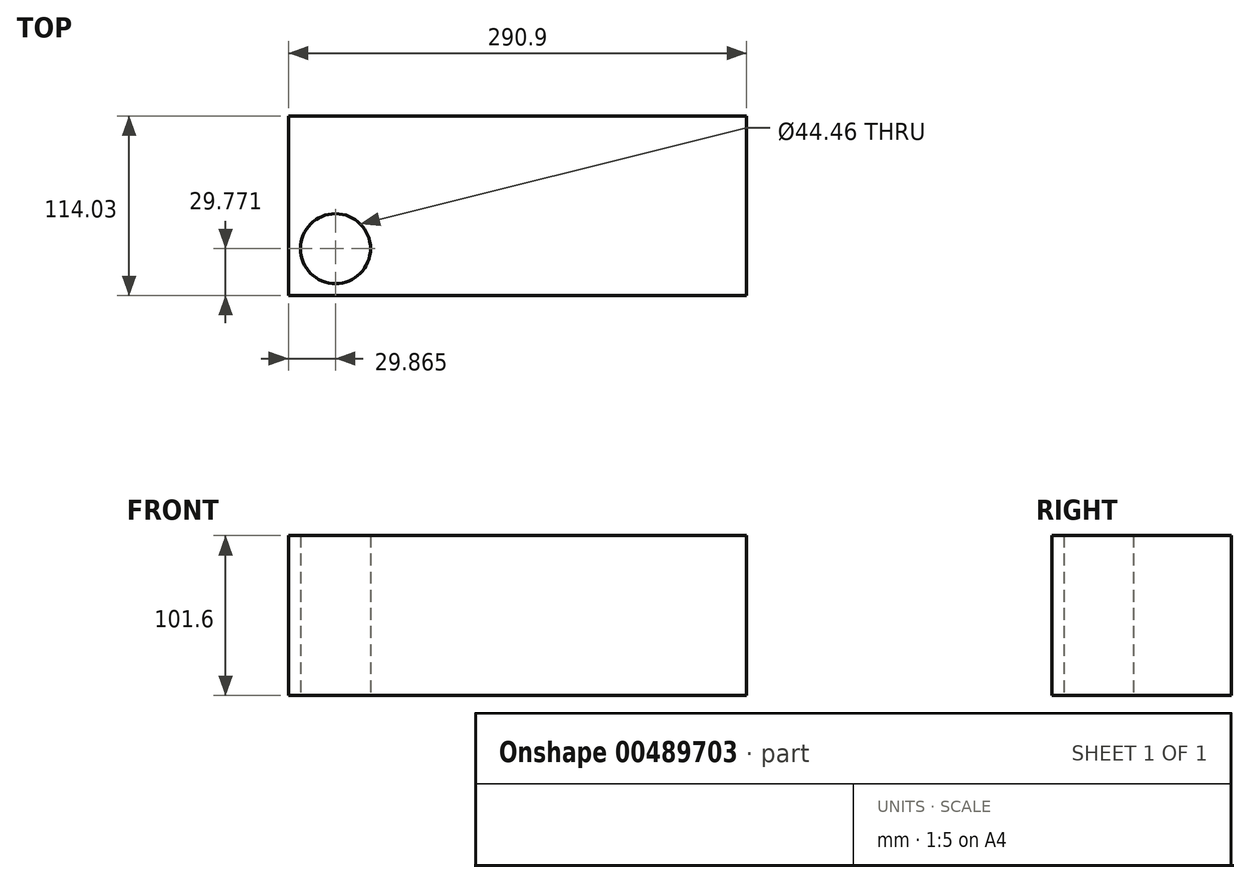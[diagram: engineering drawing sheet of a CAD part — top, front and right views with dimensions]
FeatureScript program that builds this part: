
annotation { "Feature Type Name" : "Feature", "Feature Type Description" : "" }
export const myFeature = defineFeature(function(context is Context, id is Id, definition is map)
    precondition{}
    {
        {
            var Q0;
            Q0=qCreatedBy(makeId("Top.planeOp"),FACE);
            var sketch = newSketch(context, id + "F0", { "sketchPlane" : qUnion([Q0])});
            skLineSegment(sketch, "E0.bottom", {"start": v(-66.27, 50.65) * mm, "end": v(224.63, 50.65) * mm});
            skLineSegment(sketch, "E0.top", {"start": v(-66.27, -63.38) * mm, "end": v(224.63, -63.38) * mm});
            skLineSegment(sketch, "E0.left", {"start": v(-66.27, 50.65) * mm, "end": v(-66.27, -63.38) * mm});
            skLineSegment(sketch, "E0.right", {"start": v(224.63, 50.65) * mm, "end": v(224.63, -63.38) * mm});
            skCircle(sketch, "E1", {"center": v(-36.4, -33.6) * mm, "radius": 22.23 * mm});
            skSolve(sketch);
        }
        {
            var Q0;
            Q0=makeQuery(id+"F0.imprint","IMPRINT",FACE,{"disambiguationData":[TD([[makeQuery(id+"F0.imprint","IMPRINT",EDGE,{"derivedFrom":sQuery(id+"F0.wireOp",EDGE,"E0.bottom")}),-1.0]])]});
            extrude(context, id + "F1", {"entities" : qUnion([Q0]), "depth" : 101.6 * mm});
        }
        {
            var Q0;
            Q0=makeQuery(id+"F1.opExtrude","CAP_FACE",FACE,{"disambiguationData":[OSD([sQuery(id+"F0.wireOp",EDGE,"E0.bottom"),sQuery(id+"F0.wireOp",EDGE,"E0.top"),sQuery(id+"F0.wireOp",EDGE,"E0.left"),sQuery(id+"F0.wireOp",EDGE,"E0.right"),sQuery(id+"F0.wireOp",EDGE,"E1")])],"isStart":false});
            var sketch = newSketch(context, id + "F2", { "sketchPlane" : qUnion([Q0])});
            skLineSegment(sketch, "E2.bottom", {"start": v(90.72, 17.61) * mm, "end": v(113.67, 17.61) * mm});
            skLineSegment(sketch, "E2.left", {"start": v(90.72, 17.61) * mm, "end": v(90.72, 3.5) * mm});
            skLineSegment(sketch, "E2.right", {"start": v(113.67, 17.61) * mm, "end": v(113.67, 0.8) * mm});
            skArc(sketch, "E3", {"start": v(90.72, 3.5) * mm, "mid": v(96.88, -42.83) * mm, "end": v(113.67, 0.8) * mm});
            skSolve(sketch);
        }
        {
            var Q0;
            Q0=makeQuery(id+"F2.imprint","IMPRINT",FACE,{"disambiguationData":[TD([[makeQuery(id+"F2.imprint","IMPRINT",EDGE,{"derivedFrom":sQuery(id+"F2.wireOp",EDGE,"E2.bottom")}),-1.0]])]});
            extrude(context, id + "F3", {"entities" : qUnion([Q0]), "operationType" : NewBodyOperationType.REMOVE, "depth" : 25.4 * mm});
        }
    });
